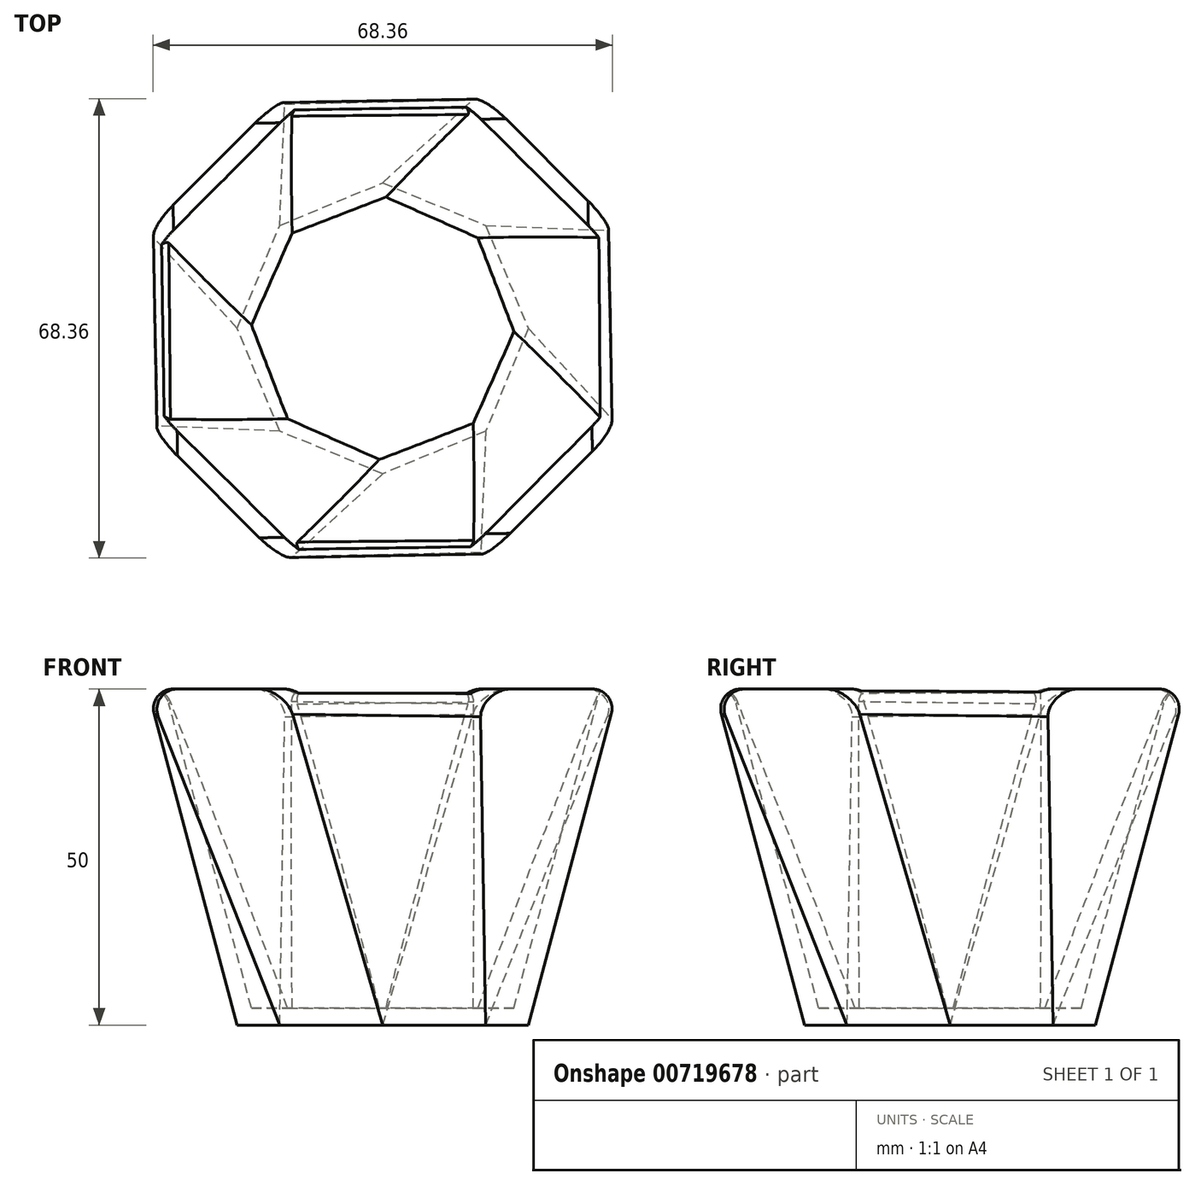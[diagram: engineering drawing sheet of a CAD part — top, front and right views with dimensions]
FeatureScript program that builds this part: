
annotation { "Feature Type Name" : "Feature", "Feature Type Description" : "" }
export const myFeature = defineFeature(function(context is Context, id is Id, definition is map)
    precondition{}
    {
        {
            var Q0;
            Q0=qCreatedBy(makeId("Top.planeOp"),FACE);
            var sketch = newSketch(context, id + "F0", { "sketchPlane" : qUnion([Q0])});
            skCircle(sketch, "E0.cCircle", {"center": v(0, 0) * mm, "radius": 35 * mm, "construction": true});
            skLineSegment(sketch, "E0.0", {"start": v(-35, -14.5) * mm, "end": v(-35, 14.5) * mm});
            skLineSegment(sketch, "E0.1", {"start": v(-35, 14.5) * mm, "end": v(-14.5, 35) * mm});
            skLineSegment(sketch, "E0.2", {"start": v(-14.5, 35) * mm, "end": v(14.5, 35) * mm});
            skLineSegment(sketch, "E0.3", {"start": v(14.5, 35) * mm, "end": v(35, 14.5) * mm});
            skLineSegment(sketch, "E0.4", {"start": v(35, 14.5) * mm, "end": v(35, -14.5) * mm});
            skLineSegment(sketch, "E0.5", {"start": v(35, -14.5) * mm, "end": v(14.5, -35) * mm});
            skLineSegment(sketch, "E0.6", {"start": v(14.5, -35) * mm, "end": v(-14.5, -35) * mm});
            skLineSegment(sketch, "E0.7", {"start": v(-14.5, -35) * mm, "end": v(-35, -14.5) * mm});
            skPoint(sketch, "E0.0.midPoint", {"position": v(-35, 0) * mm});
            skSolve(sketch);
        }
        {
            var Q0;
            Q0=qCreatedBy(makeId("Top.planeOp"),FACE);
            cPlane(context, id + "F1", {"entities" : qUnion([Q0]), "cplaneType" : CPlaneType.OFFSET, "offset" : 50 * mm, "oppositeDirection" : true, "width" : 150 * mm, "height" : 150 * mm});
        }
        {
            var Q0;
            Q0=qCreatedBy(id+"F1.planeOp",FACE);
            var sketch = newSketch(context, id + "F2", { "sketchPlane" : qUnion([Q0])});
            skCircle(sketch, "E1.cCircle", {"center": v(0, 0) * mm, "radius": 20 * mm, "construction": true});
            skLineSegment(sketch, "E1.0", {"start": v(0, 21.65) * mm, "end": v(15.3, 15.3) * mm});
            skLineSegment(sketch, "E1.1", {"start": v(15.3, 15.3) * mm, "end": v(21.65, 0) * mm});
            skLineSegment(sketch, "E1.2", {"start": v(21.65, 0) * mm, "end": v(15.3, -15.3) * mm});
            skLineSegment(sketch, "E1.3", {"start": v(15.3, -15.3) * mm, "end": v(0, -21.65) * mm});
            skLineSegment(sketch, "E1.4", {"start": v(0, -21.65) * mm, "end": v(-15.3, -15.3) * mm});
            skLineSegment(sketch, "E1.5", {"start": v(-15.3, -15.3) * mm, "end": v(-21.65, 0) * mm});
            skLineSegment(sketch, "E1.6", {"start": v(-21.65, 0) * mm, "end": v(-15.3, 15.3) * mm});
            skLineSegment(sketch, "E1.7", {"start": v(-15.3, 15.3) * mm, "end": v(0, 21.65) * mm});
            skPoint(sketch, "E1.0.midPoint", {"position": v(7.65, 18.48) * mm});
            skSolve(sketch);
        }
        {
            var Q0;
            Q0=makeQuery(id+"F2.imprint","IMPRINT",FACE,{"disambiguationData":[TD([[makeQuery(id+"F2.imprint","IMPRINT",EDGE,{"derivedFrom":sQuery(id+"F2.wireOp",EDGE,"E1.0")}),-1.0]])]});
            var Q1;
            Q1=makeQuery(id+"F0.imprint","IMPRINT",FACE,{"disambiguationData":[TD([[makeQuery(id+"F0.imprint","IMPRINT",EDGE,{"derivedFrom":sQuery(id+"F0.wireOp",EDGE,"E0.0")}),-1.0]])]});
            loft(context, id + "F3", {"sheetProfilesArray" : [{ "sheetProfileEntities" : qUnion([Q0]) }, { "sheetProfileEntities" : qUnion([Q1]) }]});
        }
        {
            var Q0;
            Q0=makeQuery(id+"F3.opLoft","CAP_FACE",FACE,{"disambiguationData":[OSD([makeQuery(id+"F0.imprint","IMPRINT",FACE,{"disambiguationData":[TD([[makeQuery(id+"F0.imprint","IMPRINT",EDGE,{"derivedFrom":sQuery(id+"F0.wireOp",EDGE,"E0.0")}),-1.0]])]})])],"isStart":true});
            shell(context, id + "F4", {"entities" : qUnion([Q0]), "thickness" : 2.5 * mm});
        }
        {
            var Q0;
            Q0=makeQuery(id+"F4.opShell","OFFSET_EDGE",EDGE,{"disambiguationData":[OSD([sQuery(id+"F0.wireOp",EDGE,"E0.5"),sQuery(id+"F0.wireOp",EDGE,"E0.6"),sQuery(id+"F0.wireOp",EDGE,"E0.7")])]});
            var Q1;
            Q1=makeQuery(id+"F4.opShell","OFFSET_EDGE",EDGE,{"disambiguationData":[OSD([sQuery(id+"F0.wireOp",EDGE,"E0.0"),sQuery(id+"F0.wireOp",EDGE,"E0.1"),sQuery(id+"F0.wireOp",EDGE,"E0.7")])]});
            var Q2;
            Q2=makeQuery(id+"F4.opShell","OFFSET_EDGE",EDGE,{"disambiguationData":[OSD([sQuery(id+"F0.wireOp",EDGE,"E0.1"),sQuery(id+"F0.wireOp",EDGE,"E0.2"),sQuery(id+"F0.wireOp",EDGE,"E0.3")])]});
            var Q3;
            Q3=makeQuery(id+"F3.opLoft","MID_CAP_EDGE",EDGE,{"disambiguationData":[OSD([sQuery(id+"F0.wireOp",EDGE,"E0.3"),sQuery(id+"F0.wireOp",EDGE,"E0.4"),sQuery(id+"F0.wireOp",EDGE,"E0.5")])],"capPos":1.0});
            fillet(context, id + "F5", {"entities" : qUnion([Q0, Q1, Q2, Q3]), "radius" : 3 * mm, "tangentPropagation" : true, "allowEdgeOverflow" : false});
        }
        {
            var Q0;
            Q0=makeQuery(id+"F3.opLoft","MID_CAP_EDGE",EDGE,{"disambiguationData":[OSD([sQuery(id+"F0.wireOp",EDGE,"E0.1"),sQuery(id+"F0.wireOp",EDGE,"E0.2"),sQuery(id+"F0.wireOp",EDGE,"E0.3")])],"capPos":1.0});
            var Q1;
            Q1=makeQuery(id+"F3.opLoft","MID_CAP_EDGE",EDGE,{"disambiguationData":[OSD([sQuery(id+"F0.wireOp",EDGE,"E0.0"),sQuery(id+"F0.wireOp",EDGE,"E0.1"),sQuery(id+"F0.wireOp",EDGE,"E0.7")])],"capPos":1.0});
            var Q2;
            Q2=makeQuery(id+"F3.opLoft","MID_CAP_EDGE",EDGE,{"disambiguationData":[OSD([sQuery(id+"F0.wireOp",EDGE,"E0.5"),sQuery(id+"F0.wireOp",EDGE,"E0.6"),sQuery(id+"F0.wireOp",EDGE,"E0.7")])],"capPos":1.0});
            fillet(context, id + "F6", {"entities" : qUnion([Q0, Q1, Q2]), "radius" : 3 * mm, "tangentPropagation" : true, "allowEdgeOverflow" : false});
        }
    });
